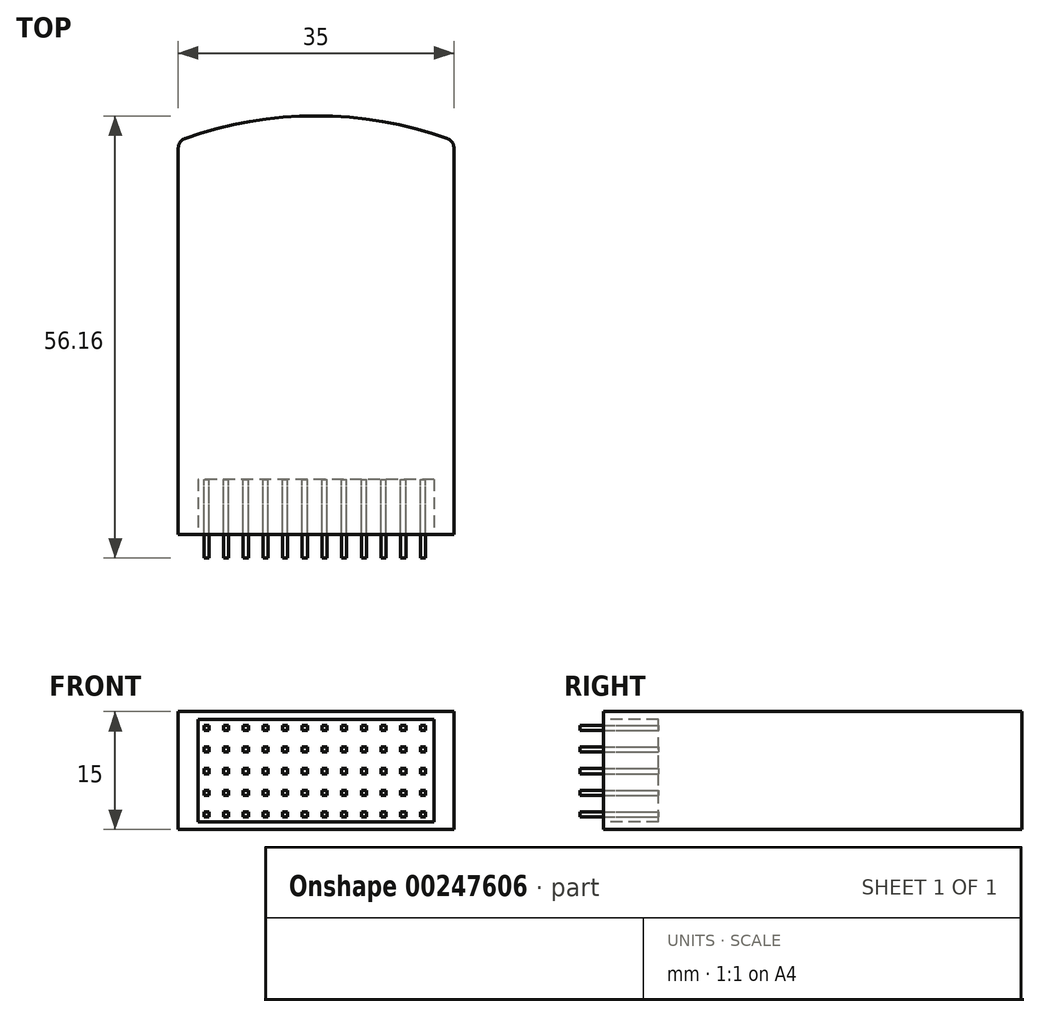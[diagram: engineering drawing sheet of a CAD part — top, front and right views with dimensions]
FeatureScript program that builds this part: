
annotation { "Feature Type Name" : "Feature", "Feature Type Description" : "" }
export const myFeature = defineFeature(function(context is Context, id is Id, definition is map)
    precondition{}
    {
        {
            var Q0;
            Q0=qCreatedBy(makeId("Top.planeOp"),FACE);
            var sketch = newSketch(context, id + "F0", { "sketchPlane" : qUnion([Q0])});
            skLineSegment(sketch, "E0.bottom", {"start": v(17.5, -25) * mm, "end": v(-17.5, -25) * mm});
            skLineSegment(sketch, "E0.top", {"start": v(17.5, 25) * mm, "end": v(-17.5, 25) * mm});
            skLineSegment(sketch, "E0.left", {"start": v(17.5, -25) * mm, "end": v(17.5, 25) * mm});
            skLineSegment(sketch, "E0.right", {"start": v(-17.5, -25) * mm, "end": v(-17.5, 25) * mm});
            skPoint(sketch, "E0.middle", {"position": v(0, 0) * mm});
            skPoint(sketch, "E1.startSnap0", {"position": v(0, 25) * mm});
            skArc(sketch, "E2", {"start": v(17.5, 25) * mm, "mid": v(0, 28.16) * mm, "end": v(-17.5, 25) * mm});
            skSolve(sketch);
        }
        {
            var Q0;
            Q0=qSketchRegion(id+"F0",true);
            extrude(context, id + "F1", {"entities" : qUnion([Q0]), "depth" : 15 * mm, "symmetric" : true});
        }
        {
            var Q0;
            Q0=makeQuery(id+"F1.opExtrude","SWEPT_EDGE",EDGE,{"disambiguationData":[OSD([sQuery(id+"F0.wireOp",EDGE,"E0.top"),sQuery(id+"F0.wireOp",EDGE,"E0.left"),sQuery(id+"F0.wireOp",EDGE,"yyNhz9fe-Qt3a-qb7e-cI5q-L0wKWxCpfobD")])]});
            var Q1;
            Q1=makeQuery(id+"F1.opExtrude","SWEPT_EDGE",EDGE,{"disambiguationData":[OSD([sQuery(id+"F0.wireOp",EDGE,"E0.top"),sQuery(id+"F0.wireOp",EDGE,"E0.right"),sQuery(id+"F0.wireOp",EDGE,"NXXVwKCm-iX8Y-aLn6-gdMx-Pbhs1YLQSOhg")])]});
            fillet(context, id + "F2", {"entities" : qUnion([Q0, Q1]), "radius" : 1.25 * mm, "tangentPropagation" : true, "allowEdgeOverflow" : false});
        }
        {
            var Q0;
            Q0=makeQuery(id+"F1.opExtrude","SWEPT_FACE",FACE,{"disambiguationData":[OSD([sQuery(id+"F0.wireOp",EDGE,"E0.bottom")])]});
            var sketch = newSketch(context, id + "F3", { "sketchPlane" : qUnion([Q0])});
            skPoint(sketch, "E3.0", {"position": v(0, 0) * mm});
            skLineSegment(sketch, "E4.bottom", {"start": v(15, -6.5) * mm, "end": v(-15, -6.5) * mm});
            skLineSegment(sketch, "E4.top", {"start": v(15, 6.5) * mm, "end": v(-15, 6.5) * mm});
            skLineSegment(sketch, "E4.left", {"start": v(15, -6.5) * mm, "end": v(15, 6.5) * mm});
            skLineSegment(sketch, "E4.right", {"start": v(-15, -6.5) * mm, "end": v(-15, 6.5) * mm});
            skSolve(sketch);
        }
        {
            var Q0;
            Q0=qSketchRegion(id+"F3",true);
            extrude(context, id + "F4", {"entities" : qUnion([Q0]), "operationType" : NewBodyOperationType.REMOVE, "oppositeDirection" : true, "depth" : 7 * mm});
        }
        {
            var Q0;
            Q0=makeQuery(id+"F4.boolean.opBoolean","COPY",FACE,{"derivedFrom":makeQuery(id+"F4.opExtrude","CAP_FACE",FACE,{"disambiguationData":[OSD([sQuery(id+"F3.wireOp",EDGE,"E4.bottom"),sQuery(id+"F3.wireOp",EDGE,"E4.top"),sQuery(id+"F3.wireOp",EDGE,"E4.left"),sQuery(id+"F3.wireOp",EDGE,"E4.right")])],"isStart":false})});
            var sketch = newSketch(context, id + "F5", { "sketchPlane" : qUnion([Q0])});
            skLineSegment(sketch, "E5.bottom", {"start": v(-14.25, 5.75) * mm, "end": v(-13.6, 5.75) * mm});
            skLineSegment(sketch, "E5.top", {"start": v(-14.25, 5.1) * mm, "end": v(-13.6, 5.1) * mm});
            skLineSegment(sketch, "E5.left", {"start": v(-14.25, 5.75) * mm, "end": v(-14.25, 5.1) * mm});
            skLineSegment(sketch, "E5.right", {"start": v(-13.6, 5.75) * mm, "end": v(-13.6, 5.1) * mm});
            skLineSegment(sketch, "E6.1.0.0", {"start": v(-11.75, 5.75) * mm, "end": v(-11.1, 5.75) * mm});
            skLineSegment(sketch, "E6.1.0.1", {"start": v(-11.75, 5.75) * mm, "end": v(-11.75, 5.1) * mm});
            skLineSegment(sketch, "E6.1.0.2", {"start": v(-11.75, 5.1) * mm, "end": v(-11.1, 5.1) * mm});
            skLineSegment(sketch, "E6.1.0.3", {"start": v(-11.1, 5.75) * mm, "end": v(-11.1, 5.1) * mm});
            skLineSegment(sketch, "E6.2.0.0", {"start": v(-9.25, 5.75) * mm, "end": v(-8.6, 5.75) * mm});
            skLineSegment(sketch, "E6.2.0.1", {"start": v(-9.25, 5.75) * mm, "end": v(-9.25, 5.1) * mm});
            skLineSegment(sketch, "E6.2.0.2", {"start": v(-9.25, 5.1) * mm, "end": v(-8.6, 5.1) * mm});
            skLineSegment(sketch, "E6.2.0.3", {"start": v(-8.6, 5.75) * mm, "end": v(-8.6, 5.1) * mm});
            skLineSegment(sketch, "E6.3.0.0", {"start": v(-6.75, 5.75) * mm, "end": v(-6.1, 5.75) * mm});
            skLineSegment(sketch, "E6.3.0.1", {"start": v(-6.75, 5.75) * mm, "end": v(-6.75, 5.1) * mm});
            skLineSegment(sketch, "E6.3.0.2", {"start": v(-6.75, 5.1) * mm, "end": v(-6.1, 5.1) * mm});
            skLineSegment(sketch, "E6.3.0.3", {"start": v(-6.1, 5.75) * mm, "end": v(-6.1, 5.1) * mm});
            skLineSegment(sketch, "E6.4.0.0", {"start": v(-4.25, 5.75) * mm, "end": v(-3.6, 5.75) * mm});
            skLineSegment(sketch, "E6.4.0.1", {"start": v(-4.25, 5.75) * mm, "end": v(-4.25, 5.1) * mm});
            skLineSegment(sketch, "E6.4.0.2", {"start": v(-4.25, 5.1) * mm, "end": v(-3.6, 5.1) * mm});
            skLineSegment(sketch, "E6.4.0.3", {"start": v(-3.6, 5.75) * mm, "end": v(-3.6, 5.1) * mm});
            skLineSegment(sketch, "E6.5.0.0", {"start": v(-1.75, 5.75) * mm, "end": v(-1.1, 5.75) * mm});
            skLineSegment(sketch, "E6.5.0.1", {"start": v(-1.75, 5.75) * mm, "end": v(-1.75, 5.1) * mm});
            skLineSegment(sketch, "E6.5.0.2", {"start": v(-1.75, 5.1) * mm, "end": v(-1.1, 5.1) * mm});
            skLineSegment(sketch, "E6.5.0.3", {"start": v(-1.1, 5.75) * mm, "end": v(-1.1, 5.1) * mm});
            skLineSegment(sketch, "E6.6.0.0", {"start": v(0.75, 5.75) * mm, "end": v(1.4, 5.75) * mm});
            skLineSegment(sketch, "E6.6.0.1", {"start": v(0.75, 5.75) * mm, "end": v(0.75, 5.1) * mm});
            skLineSegment(sketch, "E6.6.0.2", {"start": v(0.75, 5.1) * mm, "end": v(1.4, 5.1) * mm});
            skLineSegment(sketch, "E6.6.0.3", {"start": v(1.4, 5.75) * mm, "end": v(1.4, 5.1) * mm});
            skLineSegment(sketch, "E6.7.0.0", {"start": v(3.25, 5.75) * mm, "end": v(3.9, 5.75) * mm});
            skLineSegment(sketch, "E6.7.0.1", {"start": v(3.25, 5.75) * mm, "end": v(3.25, 5.1) * mm});
            skLineSegment(sketch, "E6.7.0.2", {"start": v(3.25, 5.1) * mm, "end": v(3.9, 5.1) * mm});
            skLineSegment(sketch, "E6.7.0.3", {"start": v(3.9, 5.75) * mm, "end": v(3.9, 5.1) * mm});
            skLineSegment(sketch, "E6.8.0.0", {"start": v(5.75, 5.75) * mm, "end": v(6.4, 5.75) * mm});
            skLineSegment(sketch, "E6.8.0.1", {"start": v(5.75, 5.75) * mm, "end": v(5.75, 5.1) * mm});
            skLineSegment(sketch, "E6.8.0.2", {"start": v(5.75, 5.1) * mm, "end": v(6.4, 5.1) * mm});
            skLineSegment(sketch, "E6.8.0.3", {"start": v(6.4, 5.75) * mm, "end": v(6.4, 5.1) * mm});
            skLineSegment(sketch, "E6.9.0.0", {"start": v(8.25, 5.75) * mm, "end": v(8.9, 5.75) * mm});
            skLineSegment(sketch, "E6.9.0.1", {"start": v(8.25, 5.75) * mm, "end": v(8.25, 5.1) * mm});
            skLineSegment(sketch, "E6.9.0.2", {"start": v(8.25, 5.1) * mm, "end": v(8.9, 5.1) * mm});
            skLineSegment(sketch, "E6.9.0.3", {"start": v(8.9, 5.75) * mm, "end": v(8.9, 5.1) * mm});
            skLineSegment(sketch, "E6.10.0.0", {"start": v(10.75, 5.75) * mm, "end": v(11.4, 5.75) * mm});
            skLineSegment(sketch, "E6.10.0.1", {"start": v(10.75, 5.75) * mm, "end": v(10.75, 5.1) * mm});
            skLineSegment(sketch, "E6.10.0.2", {"start": v(10.75, 5.1) * mm, "end": v(11.4, 5.1) * mm});
            skLineSegment(sketch, "E6.10.0.3", {"start": v(11.4, 5.75) * mm, "end": v(11.4, 5.1) * mm});
            skLineSegment(sketch, "E6.direction1", {"start": v(-14.25, 5.75) * mm, "end": v(-11.75, 5.75) * mm, "construction": true});
            skLineSegment(sketch, "E7.0.11.0", {"start": v(13.25, 5.75) * mm, "end": v(13.9, 5.75) * mm});
            skLineSegment(sketch, "E7.3.11.0", {"start": v(13.25, 5.75) * mm, "end": v(13.25, 5.1) * mm});
            skLineSegment(sketch, "E7.6.11.0", {"start": v(13.25, 5.1) * mm, "end": v(13.9, 5.1) * mm});
            skLineSegment(sketch, "E7.9.11.0", {"start": v(13.9, 5.75) * mm, "end": v(13.9, 5.1) * mm});
            skLineSegment(sketch, "E8.1.0.0", {"start": v(0.75, 3) * mm, "end": v(0.75, 2.35) * mm});
            skLineSegment(sketch, "E8.1.0.1", {"start": v(-6.75, 3) * mm, "end": v(-6.1, 3) * mm});
            skLineSegment(sketch, "E8.1.0.2", {"start": v(10.75, 3) * mm, "end": v(10.75, 2.35) * mm});
            skLineSegment(sketch, "E8.1.0.3", {"start": v(5.75, 2.35) * mm, "end": v(6.4, 2.35) * mm});
            skLineSegment(sketch, "E8.1.0.4", {"start": v(-4.25, 2.35) * mm, "end": v(-3.6, 2.35) * mm});
            skLineSegment(sketch, "E8.1.0.5", {"start": v(3.9, 3) * mm, "end": v(3.9, 2.35) * mm});
            skLineSegment(sketch, "E8.1.0.6", {"start": v(8.25, 2.35) * mm, "end": v(8.9, 2.35) * mm});
            skLineSegment(sketch, "E8.1.0.7", {"start": v(13.25, 2.35) * mm, "end": v(13.9, 2.35) * mm});
            skLineSegment(sketch, "E8.1.0.8", {"start": v(-1.75, 2.35) * mm, "end": v(-1.1, 2.35) * mm});
            skLineSegment(sketch, "E8.1.0.9", {"start": v(-8.6, 3) * mm, "end": v(-8.6, 2.35) * mm});
            skLineSegment(sketch, "E8.1.0.10", {"start": v(-9.25, 2.35) * mm, "end": v(-8.6, 2.35) * mm});
            skLineSegment(sketch, "E8.1.0.11", {"start": v(-9.25, 3) * mm, "end": v(-9.25, 2.35) * mm});
            skLineSegment(sketch, "E8.1.0.12", {"start": v(-9.25, 3) * mm, "end": v(-8.6, 3) * mm});
            skLineSegment(sketch, "E8.1.0.13", {"start": v(-11.1, 3) * mm, "end": v(-11.1, 2.35) * mm});
            skLineSegment(sketch, "E8.1.0.14", {"start": v(-11.75, 2.35) * mm, "end": v(-11.1, 2.35) * mm});
            skLineSegment(sketch, "E8.1.0.15", {"start": v(-11.75, 3) * mm, "end": v(-11.75, 2.35) * mm});
            skLineSegment(sketch, "E8.1.0.16", {"start": v(-11.75, 3) * mm, "end": v(-11.1, 3) * mm});
            skLineSegment(sketch, "E8.1.0.17", {"start": v(-13.6, 3) * mm, "end": v(-13.6, 2.35) * mm});
            skLineSegment(sketch, "E8.1.0.18", {"start": v(-14.25, 3) * mm, "end": v(-14.25, 2.35) * mm});
            skLineSegment(sketch, "E8.1.0.19", {"start": v(-14.25, 2.35) * mm, "end": v(-13.6, 2.35) * mm});
            skLineSegment(sketch, "E8.1.0.20", {"start": v(-4.25, 3) * mm, "end": v(-4.25, 2.35) * mm});
            skLineSegment(sketch, "E8.1.0.21", {"start": v(-6.1, 3) * mm, "end": v(-6.1, 2.35) * mm});
            skLineSegment(sketch, "E8.1.0.22", {"start": v(8.25, 3) * mm, "end": v(8.25, 2.35) * mm});
            skLineSegment(sketch, "E8.1.0.23", {"start": v(3.25, 2.35) * mm, "end": v(3.9, 2.35) * mm});
            skLineSegment(sketch, "E8.1.0.24", {"start": v(13.25, 3) * mm, "end": v(13.25, 2.35) * mm});
            skLineSegment(sketch, "E8.1.0.25", {"start": v(-6.75, 2.35) * mm, "end": v(-6.1, 2.35) * mm});
            skLineSegment(sketch, "E8.1.0.26", {"start": v(-1.75, 3) * mm, "end": v(-1.75, 2.35) * mm});
            skLineSegment(sketch, "E8.1.0.27", {"start": v(-6.75, 3) * mm, "end": v(-6.75, 2.35) * mm});
            skLineSegment(sketch, "E8.1.0.28", {"start": v(0.75, 3) * mm, "end": v(1.4, 3) * mm});
            skLineSegment(sketch, "E8.1.0.29", {"start": v(10.75, 3) * mm, "end": v(11.4, 3) * mm});
            skLineSegment(sketch, "E8.1.0.30", {"start": v(3.25, 3) * mm, "end": v(3.9, 3) * mm});
            skLineSegment(sketch, "E8.1.0.31", {"start": v(-14.25, 3) * mm, "end": v(-11.75, 3) * mm, "construction": true});
            skLineSegment(sketch, "E8.1.0.32", {"start": v(5.75, 3) * mm, "end": v(5.75, 2.35) * mm});
            skLineSegment(sketch, "E8.1.0.33", {"start": v(-1.1, 3) * mm, "end": v(-1.1, 2.35) * mm});
            skLineSegment(sketch, "E8.1.0.34", {"start": v(8.9, 3) * mm, "end": v(8.9, 2.35) * mm});
            skLineSegment(sketch, "E8.1.0.35", {"start": v(8.25, 3) * mm, "end": v(8.9, 3) * mm});
            skLineSegment(sketch, "E8.1.0.36", {"start": v(3.25, 3) * mm, "end": v(3.25, 2.35) * mm});
            skLineSegment(sketch, "E8.1.0.37", {"start": v(13.25, 3) * mm, "end": v(13.9, 3) * mm});
            skLineSegment(sketch, "E8.1.0.38", {"start": v(-1.75, 3) * mm, "end": v(-1.1, 3) * mm});
            skLineSegment(sketch, "E8.1.0.39", {"start": v(1.4, 3) * mm, "end": v(1.4, 2.35) * mm});
            skLineSegment(sketch, "E8.1.0.40", {"start": v(11.4, 3) * mm, "end": v(11.4, 2.35) * mm});
            skLineSegment(sketch, "E8.1.0.41", {"start": v(5.75, 3) * mm, "end": v(6.4, 3) * mm});
            skLineSegment(sketch, "E8.1.0.42", {"start": v(13.9, 3) * mm, "end": v(13.9, 2.35) * mm});
            skLineSegment(sketch, "E8.1.0.43", {"start": v(-4.25, 3) * mm, "end": v(-3.6, 3) * mm});
            skLineSegment(sketch, "E8.1.0.44", {"start": v(6.4, 3) * mm, "end": v(6.4, 2.35) * mm});
            skLineSegment(sketch, "E8.1.0.45", {"start": v(-3.6, 3) * mm, "end": v(-3.6, 2.35) * mm});
            skLineSegment(sketch, "E8.1.0.46", {"start": v(0.75, 2.35) * mm, "end": v(1.4, 2.35) * mm});
            skLineSegment(sketch, "E8.1.0.47", {"start": v(10.75, 2.35) * mm, "end": v(11.4, 2.35) * mm});
            skLineSegment(sketch, "E8.1.0.48", {"start": v(-14.25, 3) * mm, "end": v(-13.6, 3) * mm});
            skLineSegment(sketch, "E8.2.0.0", {"start": v(0.75, 0.25) * mm, "end": v(0.75, -0.4) * mm});
            skLineSegment(sketch, "E8.2.0.1", {"start": v(-6.75, 0.25) * mm, "end": v(-6.1, 0.25) * mm});
            skLineSegment(sketch, "E8.2.0.2", {"start": v(10.75, 0.25) * mm, "end": v(10.75, -0.4) * mm});
            skLineSegment(sketch, "E8.2.0.3", {"start": v(5.75, -0.4) * mm, "end": v(6.4, -0.4) * mm});
            skLineSegment(sketch, "E8.2.0.4", {"start": v(-4.25, -0.4) * mm, "end": v(-3.6, -0.4) * mm});
            skLineSegment(sketch, "E8.2.0.5", {"start": v(3.9, 0.25) * mm, "end": v(3.9, -0.4) * mm});
            skLineSegment(sketch, "E8.2.0.6", {"start": v(8.25, -0.4) * mm, "end": v(8.9, -0.4) * mm});
            skLineSegment(sketch, "E8.2.0.7", {"start": v(13.25, -0.4) * mm, "end": v(13.9, -0.4) * mm});
            skLineSegment(sketch, "E8.2.0.8", {"start": v(-1.75, -0.4) * mm, "end": v(-1.1, -0.4) * mm});
            skLineSegment(sketch, "E8.2.0.9", {"start": v(-8.6, 0.25) * mm, "end": v(-8.6, -0.4) * mm});
            skLineSegment(sketch, "E8.2.0.10", {"start": v(-9.25, -0.4) * mm, "end": v(-8.6, -0.4) * mm});
            skLineSegment(sketch, "E8.2.0.11", {"start": v(-9.25, 0.25) * mm, "end": v(-9.25, -0.4) * mm});
            skLineSegment(sketch, "E8.2.0.12", {"start": v(-9.25, 0.25) * mm, "end": v(-8.6, 0.25) * mm});
            skLineSegment(sketch, "E8.2.0.13", {"start": v(-11.1, 0.25) * mm, "end": v(-11.1, -0.4) * mm});
            skLineSegment(sketch, "E8.2.0.14", {"start": v(-11.75, -0.4) * mm, "end": v(-11.1, -0.4) * mm});
            skLineSegment(sketch, "E8.2.0.15", {"start": v(-11.75, 0.25) * mm, "end": v(-11.75, -0.4) * mm});
            skLineSegment(sketch, "E8.2.0.16", {"start": v(-11.75, 0.25) * mm, "end": v(-11.1, 0.25) * mm});
            skLineSegment(sketch, "E8.2.0.17", {"start": v(-13.6, 0.25) * mm, "end": v(-13.6, -0.4) * mm});
            skLineSegment(sketch, "E8.2.0.18", {"start": v(-14.25, 0.25) * mm, "end": v(-14.25, -0.4) * mm});
            skLineSegment(sketch, "E8.2.0.19", {"start": v(-14.25, -0.4) * mm, "end": v(-13.6, -0.4) * mm});
            skLineSegment(sketch, "E8.2.0.20", {"start": v(-4.25, 0.25) * mm, "end": v(-4.25, -0.4) * mm});
            skLineSegment(sketch, "E8.2.0.21", {"start": v(-6.1, 0.25) * mm, "end": v(-6.1, -0.4) * mm});
            skLineSegment(sketch, "E8.2.0.22", {"start": v(8.25, 0.25) * mm, "end": v(8.25, -0.4) * mm});
            skLineSegment(sketch, "E8.2.0.23", {"start": v(3.25, -0.4) * mm, "end": v(3.9, -0.4) * mm});
            skLineSegment(sketch, "E8.2.0.24", {"start": v(13.25, 0.25) * mm, "end": v(13.25, -0.4) * mm});
            skLineSegment(sketch, "E8.2.0.25", {"start": v(-6.75, -0.4) * mm, "end": v(-6.1, -0.4) * mm});
            skLineSegment(sketch, "E8.2.0.26", {"start": v(-1.75, 0.25) * mm, "end": v(-1.75, -0.4) * mm});
            skLineSegment(sketch, "E8.2.0.27", {"start": v(-6.75, 0.25) * mm, "end": v(-6.75, -0.4) * mm});
            skLineSegment(sketch, "E8.2.0.28", {"start": v(0.75, 0.25) * mm, "end": v(1.4, 0.25) * mm});
            skLineSegment(sketch, "E8.2.0.29", {"start": v(10.75, 0.25) * mm, "end": v(11.4, 0.25) * mm});
            skLineSegment(sketch, "E8.2.0.30", {"start": v(3.25, 0.25) * mm, "end": v(3.9, 0.25) * mm});
            skLineSegment(sketch, "E8.2.0.31", {"start": v(-14.25, 0.25) * mm, "end": v(-11.75, 0.25) * mm, "construction": true});
            skLineSegment(sketch, "E8.2.0.32", {"start": v(5.75, 0.25) * mm, "end": v(5.75, -0.4) * mm});
            skLineSegment(sketch, "E8.2.0.33", {"start": v(-1.1, 0.25) * mm, "end": v(-1.1, -0.4) * mm});
            skLineSegment(sketch, "E8.2.0.34", {"start": v(8.9, 0.25) * mm, "end": v(8.9, -0.4) * mm});
            skLineSegment(sketch, "E8.2.0.35", {"start": v(8.25, 0.25) * mm, "end": v(8.9, 0.25) * mm});
            skLineSegment(sketch, "E8.2.0.36", {"start": v(3.25, 0.25) * mm, "end": v(3.25, -0.4) * mm});
            skLineSegment(sketch, "E8.2.0.37", {"start": v(13.25, 0.25) * mm, "end": v(13.9, 0.25) * mm});
            skLineSegment(sketch, "E8.2.0.38", {"start": v(-1.75, 0.25) * mm, "end": v(-1.1, 0.25) * mm});
            skLineSegment(sketch, "E8.2.0.39", {"start": v(1.4, 0.25) * mm, "end": v(1.4, -0.4) * mm});
            skLineSegment(sketch, "E8.2.0.40", {"start": v(11.4, 0.25) * mm, "end": v(11.4, -0.4) * mm});
            skLineSegment(sketch, "E8.2.0.41", {"start": v(5.75, 0.25) * mm, "end": v(6.4, 0.25) * mm});
            skLineSegment(sketch, "E8.2.0.42", {"start": v(13.9, 0.25) * mm, "end": v(13.9, -0.4) * mm});
            skLineSegment(sketch, "E8.2.0.43", {"start": v(-4.25, 0.25) * mm, "end": v(-3.6, 0.25) * mm});
            skLineSegment(sketch, "E8.2.0.44", {"start": v(6.4, 0.25) * mm, "end": v(6.4, -0.4) * mm});
            skLineSegment(sketch, "E8.2.0.45", {"start": v(-3.6, 0.25) * mm, "end": v(-3.6, -0.4) * mm});
            skLineSegment(sketch, "E8.2.0.46", {"start": v(0.75, -0.4) * mm, "end": v(1.4, -0.4) * mm});
            skLineSegment(sketch, "E8.2.0.47", {"start": v(10.75, -0.4) * mm, "end": v(11.4, -0.4) * mm});
            skLineSegment(sketch, "E8.2.0.48", {"start": v(-14.25, 0.25) * mm, "end": v(-13.6, 0.25) * mm});
            skLineSegment(sketch, "E8.3.0.0", {"start": v(0.75, -2.5) * mm, "end": v(0.75, -3.15) * mm});
            skLineSegment(sketch, "E8.3.0.1", {"start": v(-6.75, -2.5) * mm, "end": v(-6.1, -2.5) * mm});
            skLineSegment(sketch, "E8.3.0.2", {"start": v(10.75, -2.5) * mm, "end": v(10.75, -3.15) * mm});
            skLineSegment(sketch, "E8.3.0.3", {"start": v(5.75, -3.15) * mm, "end": v(6.4, -3.15) * mm});
            skLineSegment(sketch, "E8.3.0.4", {"start": v(-4.25, -3.15) * mm, "end": v(-3.6, -3.15) * mm});
            skLineSegment(sketch, "E8.3.0.5", {"start": v(3.9, -2.5) * mm, "end": v(3.9, -3.15) * mm});
            skLineSegment(sketch, "E8.3.0.6", {"start": v(8.25, -3.15) * mm, "end": v(8.9, -3.15) * mm});
            skLineSegment(sketch, "E8.3.0.7", {"start": v(13.25, -3.15) * mm, "end": v(13.9, -3.15) * mm});
            skLineSegment(sketch, "E8.3.0.8", {"start": v(-1.75, -3.15) * mm, "end": v(-1.1, -3.15) * mm});
            skLineSegment(sketch, "E8.3.0.9", {"start": v(-8.6, -2.5) * mm, "end": v(-8.6, -3.15) * mm});
            skLineSegment(sketch, "E8.3.0.10", {"start": v(-9.25, -3.15) * mm, "end": v(-8.6, -3.15) * mm});
            skLineSegment(sketch, "E8.3.0.11", {"start": v(-9.25, -2.5) * mm, "end": v(-9.25, -3.15) * mm});
            skLineSegment(sketch, "E8.3.0.12", {"start": v(-9.25, -2.5) * mm, "end": v(-8.6, -2.5) * mm});
            skLineSegment(sketch, "E8.3.0.13", {"start": v(-11.1, -2.5) * mm, "end": v(-11.1, -3.15) * mm});
            skLineSegment(sketch, "E8.3.0.14", {"start": v(-11.75, -3.15) * mm, "end": v(-11.1, -3.15) * mm});
            skLineSegment(sketch, "E8.3.0.15", {"start": v(-11.75, -2.5) * mm, "end": v(-11.75, -3.15) * mm});
            skLineSegment(sketch, "E8.3.0.16", {"start": v(-11.75, -2.5) * mm, "end": v(-11.1, -2.5) * mm});
            skLineSegment(sketch, "E8.3.0.17", {"start": v(-13.6, -2.5) * mm, "end": v(-13.6, -3.15) * mm});
            skLineSegment(sketch, "E8.3.0.18", {"start": v(-14.25, -2.5) * mm, "end": v(-14.25, -3.15) * mm});
            skLineSegment(sketch, "E8.3.0.19", {"start": v(-14.25, -3.15) * mm, "end": v(-13.6, -3.15) * mm});
            skLineSegment(sketch, "E8.3.0.20", {"start": v(-4.25, -2.5) * mm, "end": v(-4.25, -3.15) * mm});
            skLineSegment(sketch, "E8.3.0.21", {"start": v(-6.1, -2.5) * mm, "end": v(-6.1, -3.15) * mm});
            skLineSegment(sketch, "E8.3.0.22", {"start": v(8.25, -2.5) * mm, "end": v(8.25, -3.15) * mm});
            skLineSegment(sketch, "E8.3.0.23", {"start": v(3.25, -3.15) * mm, "end": v(3.9, -3.15) * mm});
            skLineSegment(sketch, "E8.3.0.24", {"start": v(13.25, -2.5) * mm, "end": v(13.25, -3.15) * mm});
            skLineSegment(sketch, "E8.3.0.25", {"start": v(-6.75, -3.15) * mm, "end": v(-6.1, -3.15) * mm});
            skLineSegment(sketch, "E8.3.0.26", {"start": v(-1.75, -2.5) * mm, "end": v(-1.75, -3.15) * mm});
            skLineSegment(sketch, "E8.3.0.27", {"start": v(-6.75, -2.5) * mm, "end": v(-6.75, -3.15) * mm});
            skLineSegment(sketch, "E8.3.0.28", {"start": v(0.75, -2.5) * mm, "end": v(1.4, -2.5) * mm});
            skLineSegment(sketch, "E8.3.0.29", {"start": v(10.75, -2.5) * mm, "end": v(11.4, -2.5) * mm});
            skLineSegment(sketch, "E8.3.0.30", {"start": v(3.25, -2.5) * mm, "end": v(3.9, -2.5) * mm});
            skLineSegment(sketch, "E8.3.0.31", {"start": v(-14.25, -2.5) * mm, "end": v(-11.75, -2.5) * mm, "construction": true});
            skLineSegment(sketch, "E8.3.0.32", {"start": v(5.75, -2.5) * mm, "end": v(5.75, -3.15) * mm});
            skLineSegment(sketch, "E8.3.0.33", {"start": v(-1.1, -2.5) * mm, "end": v(-1.1, -3.15) * mm});
            skLineSegment(sketch, "E8.3.0.34", {"start": v(8.9, -2.5) * mm, "end": v(8.9, -3.15) * mm});
            skLineSegment(sketch, "E8.3.0.35", {"start": v(8.25, -2.5) * mm, "end": v(8.9, -2.5) * mm});
            skLineSegment(sketch, "E8.3.0.36", {"start": v(3.25, -2.5) * mm, "end": v(3.25, -3.15) * mm});
            skLineSegment(sketch, "E8.3.0.37", {"start": v(13.25, -2.5) * mm, "end": v(13.9, -2.5) * mm});
            skLineSegment(sketch, "E8.3.0.38", {"start": v(-1.75, -2.5) * mm, "end": v(-1.1, -2.5) * mm});
            skLineSegment(sketch, "E8.3.0.39", {"start": v(1.4, -2.5) * mm, "end": v(1.4, -3.15) * mm});
            skLineSegment(sketch, "E8.3.0.40", {"start": v(11.4, -2.5) * mm, "end": v(11.4, -3.15) * mm});
            skLineSegment(sketch, "E8.3.0.41", {"start": v(5.75, -2.5) * mm, "end": v(6.4, -2.5) * mm});
            skLineSegment(sketch, "E8.3.0.42", {"start": v(13.9, -2.5) * mm, "end": v(13.9, -3.15) * mm});
            skLineSegment(sketch, "E8.3.0.43", {"start": v(-4.25, -2.5) * mm, "end": v(-3.6, -2.5) * mm});
            skLineSegment(sketch, "E8.3.0.44", {"start": v(6.4, -2.5) * mm, "end": v(6.4, -3.15) * mm});
            skLineSegment(sketch, "E8.3.0.45", {"start": v(-3.6, -2.5) * mm, "end": v(-3.6, -3.15) * mm});
            skLineSegment(sketch, "E8.3.0.46", {"start": v(0.75, -3.15) * mm, "end": v(1.4, -3.15) * mm});
            skLineSegment(sketch, "E8.3.0.47", {"start": v(10.75, -3.15) * mm, "end": v(11.4, -3.15) * mm});
            skLineSegment(sketch, "E8.3.0.48", {"start": v(-14.25, -2.5) * mm, "end": v(-13.6, -2.5) * mm});
            skLineSegment(sketch, "E8.4.0.0", {"start": v(0.75, -5.25) * mm, "end": v(0.75, -5.9) * mm});
            skLineSegment(sketch, "E8.4.0.1", {"start": v(-6.75, -5.25) * mm, "end": v(-6.1, -5.25) * mm});
            skLineSegment(sketch, "E8.4.0.2", {"start": v(10.75, -5.25) * mm, "end": v(10.75, -5.9) * mm});
            skLineSegment(sketch, "E8.4.0.3", {"start": v(5.75, -5.9) * mm, "end": v(6.4, -5.9) * mm});
            skLineSegment(sketch, "E8.4.0.4", {"start": v(-4.25, -5.9) * mm, "end": v(-3.6, -5.9) * mm});
            skLineSegment(sketch, "E8.4.0.5", {"start": v(3.9, -5.25) * mm, "end": v(3.9, -5.9) * mm});
            skLineSegment(sketch, "E8.4.0.6", {"start": v(8.25, -5.9) * mm, "end": v(8.9, -5.9) * mm});
            skLineSegment(sketch, "E8.4.0.7", {"start": v(13.25, -5.9) * mm, "end": v(13.9, -5.9) * mm});
            skLineSegment(sketch, "E8.4.0.8", {"start": v(-1.75, -5.9) * mm, "end": v(-1.1, -5.9) * mm});
            skLineSegment(sketch, "E8.4.0.9", {"start": v(-8.6, -5.25) * mm, "end": v(-8.6, -5.9) * mm});
            skLineSegment(sketch, "E8.4.0.10", {"start": v(-9.25, -5.9) * mm, "end": v(-8.6, -5.9) * mm});
            skLineSegment(sketch, "E8.4.0.11", {"start": v(-9.25, -5.25) * mm, "end": v(-9.25, -5.9) * mm});
            skLineSegment(sketch, "E8.4.0.12", {"start": v(-9.25, -5.25) * mm, "end": v(-8.6, -5.25) * mm});
            skLineSegment(sketch, "E8.4.0.13", {"start": v(-11.1, -5.25) * mm, "end": v(-11.1, -5.9) * mm});
            skLineSegment(sketch, "E8.4.0.14", {"start": v(-11.75, -5.9) * mm, "end": v(-11.1, -5.9) * mm});
            skLineSegment(sketch, "E8.4.0.15", {"start": v(-11.75, -5.25) * mm, "end": v(-11.75, -5.9) * mm});
            skLineSegment(sketch, "E8.4.0.16", {"start": v(-11.75, -5.25) * mm, "end": v(-11.1, -5.25) * mm});
            skLineSegment(sketch, "E8.4.0.17", {"start": v(-13.6, -5.25) * mm, "end": v(-13.6, -5.9) * mm});
            skLineSegment(sketch, "E8.4.0.18", {"start": v(-14.25, -5.25) * mm, "end": v(-14.25, -5.9) * mm});
            skLineSegment(sketch, "E8.4.0.19", {"start": v(-14.25, -5.9) * mm, "end": v(-13.6, -5.9) * mm});
            skLineSegment(sketch, "E8.4.0.20", {"start": v(-4.25, -5.25) * mm, "end": v(-4.25, -5.9) * mm});
            skLineSegment(sketch, "E8.4.0.21", {"start": v(-6.1, -5.25) * mm, "end": v(-6.1, -5.9) * mm});
            skLineSegment(sketch, "E8.4.0.22", {"start": v(8.25, -5.25) * mm, "end": v(8.25, -5.9) * mm});
            skLineSegment(sketch, "E8.4.0.23", {"start": v(3.25, -5.9) * mm, "end": v(3.9, -5.9) * mm});
            skLineSegment(sketch, "E8.4.0.24", {"start": v(13.25, -5.25) * mm, "end": v(13.25, -5.9) * mm});
            skLineSegment(sketch, "E8.4.0.25", {"start": v(-6.75, -5.9) * mm, "end": v(-6.1, -5.9) * mm});
            skLineSegment(sketch, "E8.4.0.26", {"start": v(-1.75, -5.25) * mm, "end": v(-1.75, -5.9) * mm});
            skLineSegment(sketch, "E8.4.0.27", {"start": v(-6.75, -5.25) * mm, "end": v(-6.75, -5.9) * mm});
            skLineSegment(sketch, "E8.4.0.28", {"start": v(0.75, -5.25) * mm, "end": v(1.4, -5.25) * mm});
            skLineSegment(sketch, "E8.4.0.29", {"start": v(10.75, -5.25) * mm, "end": v(11.4, -5.25) * mm});
            skLineSegment(sketch, "E8.4.0.30", {"start": v(3.25, -5.25) * mm, "end": v(3.9, -5.25) * mm});
            skLineSegment(sketch, "E8.4.0.31", {"start": v(-14.25, -5.25) * mm, "end": v(-11.75, -5.25) * mm, "construction": true});
            skLineSegment(sketch, "E8.4.0.32", {"start": v(5.75, -5.25) * mm, "end": v(5.75, -5.9) * mm});
            skLineSegment(sketch, "E8.4.0.33", {"start": v(-1.1, -5.25) * mm, "end": v(-1.1, -5.9) * mm});
            skLineSegment(sketch, "E8.4.0.34", {"start": v(8.9, -5.25) * mm, "end": v(8.9, -5.9) * mm});
            skLineSegment(sketch, "E8.4.0.35", {"start": v(8.25, -5.25) * mm, "end": v(8.9, -5.25) * mm});
            skLineSegment(sketch, "E8.4.0.36", {"start": v(3.25, -5.25) * mm, "end": v(3.25, -5.9) * mm});
            skLineSegment(sketch, "E8.4.0.37", {"start": v(13.25, -5.25) * mm, "end": v(13.9, -5.25) * mm});
            skLineSegment(sketch, "E8.4.0.38", {"start": v(-1.75, -5.25) * mm, "end": v(-1.1, -5.25) * mm});
            skLineSegment(sketch, "E8.4.0.39", {"start": v(1.4, -5.25) * mm, "end": v(1.4, -5.9) * mm});
            skLineSegment(sketch, "E8.4.0.40", {"start": v(11.4, -5.25) * mm, "end": v(11.4, -5.9) * mm});
            skLineSegment(sketch, "E8.4.0.41", {"start": v(5.75, -5.25) * mm, "end": v(6.4, -5.25) * mm});
            skLineSegment(sketch, "E8.4.0.42", {"start": v(13.9, -5.25) * mm, "end": v(13.9, -5.9) * mm});
            skLineSegment(sketch, "E8.4.0.43", {"start": v(-4.25, -5.25) * mm, "end": v(-3.6, -5.25) * mm});
            skLineSegment(sketch, "E8.4.0.44", {"start": v(6.4, -5.25) * mm, "end": v(6.4, -5.9) * mm});
            skLineSegment(sketch, "E8.4.0.45", {"start": v(-3.6, -5.25) * mm, "end": v(-3.6, -5.9) * mm});
            skLineSegment(sketch, "E8.4.0.46", {"start": v(0.75, -5.9) * mm, "end": v(1.4, -5.9) * mm});
            skLineSegment(sketch, "E8.4.0.47", {"start": v(10.75, -5.9) * mm, "end": v(11.4, -5.9) * mm});
            skLineSegment(sketch, "E8.4.0.48", {"start": v(-14.25, -5.25) * mm, "end": v(-13.6, -5.25) * mm});
            skLineSegment(sketch, "E8.direction1", {"start": v(-14.25, 5.1) * mm, "end": v(-14.25, 2.35) * mm, "construction": true});
            skSolve(sketch);
        }
        {
            var Q0;
            Q0=qSketchRegion(id+"F5",true);
            extrude(context, id + "F6", {"entities" : qUnion([Q0]), "operationType" : NewBodyOperationType.ADD, "depth" : 10 * mm});
        }
    });
